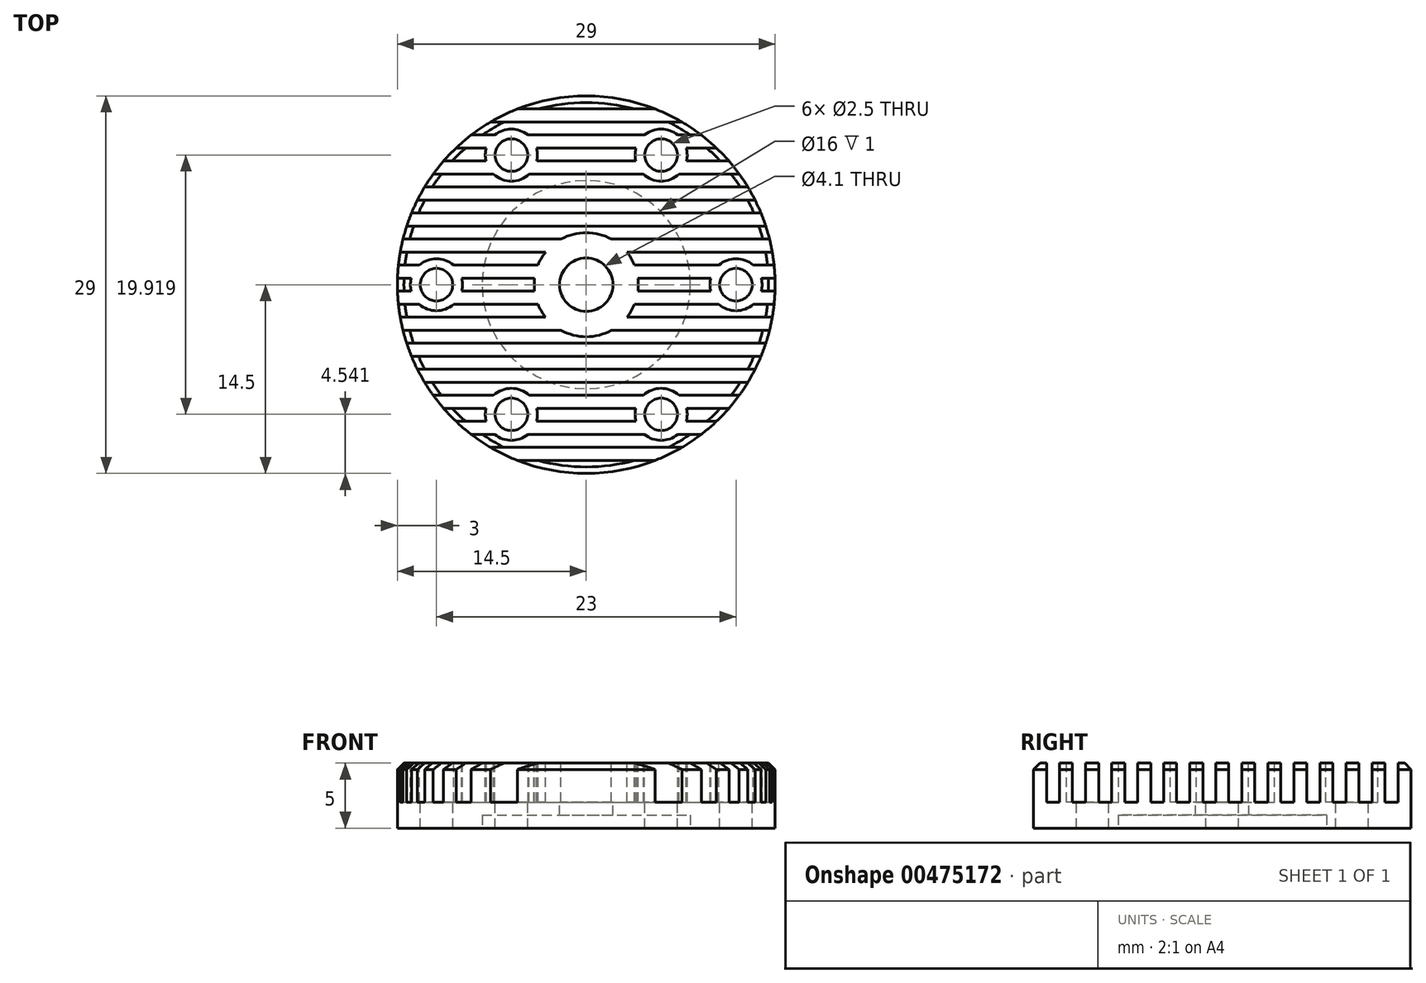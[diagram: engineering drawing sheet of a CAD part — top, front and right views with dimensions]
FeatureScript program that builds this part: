
annotation { "Feature Type Name" : "Feature", "Feature Type Description" : "" }
export const myFeature = defineFeature(function(context is Context, id is Id, definition is map)
    precondition{}
    {
        {
            var Q0;
            Q0=qCreatedBy(makeId("Top.planeOp"),FACE);
            var sketch = newSketch(context, id + "F0", { "sketchPlane" : qUnion([Q0])});
            skCircle(sketch, "E0", {"center": v(0, 0) * mm, "radius": 14.5 * mm});
            skSolve(sketch);
        }
        {
            var Q0;
            Q0 = qSketchRegion(id + "F0", true);
            extrude(context, id + "F1", {"entities" : qUnion([Q0]), "depth" : 5 * mm});
        }
        {
            var Q0;
            Q0=qCreatedBy(makeId("Right.planeOp"),FACE);
            var sketch = newSketch(context, id + "F2", { "sketchPlane" : qUnion([Q0])});
            skLineSegment(sketch, "E1", {"start": v(-0.5, 2) * mm, "end": v(-0.5, 5) * mm});
            skLineSegment(sketch, "E2", {"start": v(-0.5, 5) * mm, "end": v(0, 5) * mm});
            skLineSegment(sketch, "E3", {"start": v(-0.5, 2) * mm, "end": v(-1.5, 2) * mm});
            skLineSegment(sketch, "E4", {"start": v(-1.5, 2) * mm, "end": v(-1.5, 5) * mm});
            skLineSegment(sketch, "E5", {"start": v(-1.5, 5) * mm, "end": v(-2.5, 5) * mm});
            skLineSegment(sketch, "E6", {"start": v(-2.5, 5) * mm, "end": v(-2.5, 2) * mm});
            skLineSegment(sketch, "E7", {"start": v(-2.5, 2) * mm, "end": v(-3.5, 2) * mm});
            skLineSegment(sketch, "E8", {"start": v(-3.5, 2) * mm, "end": v(-3.5, 5) * mm});
            skLineSegment(sketch, "E9", {"start": v(-3.5, 5) * mm, "end": v(-4.5, 5) * mm});
            skLineSegment(sketch, "E10", {"start": v(-4.5, 5) * mm, "end": v(-4.5, 2) * mm});
            skLineSegment(sketch, "E11", {"start": v(-4.5, 2) * mm, "end": v(-5.5, 2) * mm});
            skLineSegment(sketch, "E12", {"start": v(-5.5, 2) * mm, "end": v(-5.5, 5) * mm});
            skLineSegment(sketch, "E13", {"start": v(-5.5, 5) * mm, "end": v(-6.5, 5) * mm});
            skLineSegment(sketch, "E14", {"start": v(-6.5, 5) * mm, "end": v(-6.5, 2) * mm});
            skLineSegment(sketch, "E15", {"start": v(-6.5, 2) * mm, "end": v(-7.5, 2) * mm});
            skLineSegment(sketch, "E16", {"start": v(-7.5, 2) * mm, "end": v(-7.5, 5) * mm});
            skLineSegment(sketch, "E17", {"start": v(-7.5, 5) * mm, "end": v(-8.5, 5) * mm});
            skLineSegment(sketch, "E18", {"start": v(-8.5, 5) * mm, "end": v(-8.5, 2) * mm});
            skLineSegment(sketch, "E19", {"start": v(-8.5, 2) * mm, "end": v(-9.5, 2) * mm});
            skLineSegment(sketch, "E20", {"start": v(-9.5, 2) * mm, "end": v(-9.5, 5) * mm});
            skLineSegment(sketch, "E21", {"start": v(-9.5, 5) * mm, "end": v(-10.5, 5) * mm});
            skLineSegment(sketch, "E22", {"start": v(-10.5, 5) * mm, "end": v(-10.5, 2) * mm});
            skLineSegment(sketch, "E23", {"start": v(-10.5, 2) * mm, "end": v(-11.5, 2) * mm});
            skLineSegment(sketch, "E24", {"start": v(-11.5, 2) * mm, "end": v(-11.5, 5) * mm});
            skLineSegment(sketch, "E25", {"start": v(-11.5, 5) * mm, "end": v(-12.5, 5) * mm});
            skLineSegment(sketch, "E26", {"start": v(-12.5, 5) * mm, "end": v(-12.5, 2) * mm});
            skLineSegment(sketch, "E27", {"start": v(-12.5, 2) * mm, "end": v(-13.5, 2) * mm});
            skLineSegment(sketch, "E28", {"start": v(-13.5, 2) * mm, "end": v(-13.5, 5) * mm});
            skLineSegment(sketch, "E29", {"start": v(-13.5, 5) * mm, "end": v(-12.5, 5) * mm});
            skLineSegment(sketch, "E30", {"start": v(-11.5, 5) * mm, "end": v(-10.5, 5) * mm});
            skLineSegment(sketch, "E31", {"start": v(-9.5, 5) * mm, "end": v(-8.5, 5) * mm});
            skLineSegment(sketch, "E32", {"start": v(-7.5, 5) * mm, "end": v(-6.5, 5) * mm});
            skLineSegment(sketch, "E33", {"start": v(-5.5, 5) * mm, "end": v(-4.5, 5) * mm});
            skLineSegment(sketch, "E34", {"start": v(-3.5, 5) * mm, "end": v(-2.5, 5) * mm});
            skLineSegment(sketch, "E35", {"start": v(-1.5, 5) * mm, "end": v(-0.5, 5) * mm});
            skLineSegment(sketch, "E36", {"start": v(0, 5) * mm, "end": v(0, 0) * mm, "construction": true});
            skLineSegment(sketch, "E37.MirrorCS", {"start": v(13.5, 5) * mm, "end": v(12.5, 5) * mm});
            skLineSegment(sketch, "E38.MirrorCS", {"start": v(13.5, 2) * mm, "end": v(13.5, 5) * mm});
            skLineSegment(sketch, "E39.MirrorCS", {"start": v(12.5, 2) * mm, "end": v(13.5, 2) * mm});
            skLineSegment(sketch, "E40.MirrorCS", {"start": v(12.5, 5) * mm, "end": v(12.5, 2) * mm});
            skLineSegment(sketch, "E41.MirrorCS", {"start": v(11.5, 5) * mm, "end": v(10.5, 5) * mm});
            skLineSegment(sketch, "E42.MirrorCS", {"start": v(11.5, 2) * mm, "end": v(11.5, 5) * mm});
            skLineSegment(sketch, "E43.MirrorCS", {"start": v(10.5, 2) * mm, "end": v(11.5, 2) * mm});
            skLineSegment(sketch, "E44.MirrorCS", {"start": v(10.5, 5) * mm, "end": v(10.5, 2) * mm});
            skLineSegment(sketch, "E45.MirrorCS", {"start": v(9.5, 5) * mm, "end": v(8.5, 5) * mm});
            skLineSegment(sketch, "E46.MirrorCS", {"start": v(9.5, 2) * mm, "end": v(9.5, 5) * mm});
            skLineSegment(sketch, "E47.MirrorCS", {"start": v(8.5, 2) * mm, "end": v(9.5, 2) * mm});
            skLineSegment(sketch, "E48.MirrorCS", {"start": v(8.5, 5) * mm, "end": v(8.5, 2) * mm});
            skLineSegment(sketch, "E49.MirrorCS", {"start": v(7.5, 5) * mm, "end": v(6.5, 5) * mm});
            skLineSegment(sketch, "E50.MirrorCS", {"start": v(7.5, 2) * mm, "end": v(7.5, 5) * mm});
            skLineSegment(sketch, "E51.MirrorCS", {"start": v(6.5, 2) * mm, "end": v(7.5, 2) * mm});
            skLineSegment(sketch, "E52.MirrorCS", {"start": v(6.5, 5) * mm, "end": v(6.5, 2) * mm});
            skLineSegment(sketch, "E53.MirrorCS", {"start": v(5.5, 5) * mm, "end": v(4.5, 5) * mm});
            skLineSegment(sketch, "E54.MirrorCS", {"start": v(5.5, 2) * mm, "end": v(5.5, 5) * mm});
            skLineSegment(sketch, "E55.MirrorCS", {"start": v(4.5, 2) * mm, "end": v(5.5, 2) * mm});
            skLineSegment(sketch, "E56.MirrorCS", {"start": v(4.5, 5) * mm, "end": v(4.5, 2) * mm});
            skLineSegment(sketch, "E57.MirrorCS", {"start": v(3.5, 5) * mm, "end": v(2.5, 5) * mm});
            skLineSegment(sketch, "E58.MirrorCS", {"start": v(3.5, 2) * mm, "end": v(3.5, 5) * mm});
            skLineSegment(sketch, "E59.MirrorCS", {"start": v(2.5, 2) * mm, "end": v(3.5, 2) * mm});
            skLineSegment(sketch, "E60.MirrorCS", {"start": v(2.5, 5) * mm, "end": v(2.5, 2) * mm});
            skLineSegment(sketch, "E61.MirrorCS", {"start": v(1.5, 5) * mm, "end": v(0.5, 5) * mm});
            skLineSegment(sketch, "E62.MirrorCS", {"start": v(1.5, 2) * mm, "end": v(1.5, 5) * mm});
            skLineSegment(sketch, "E63.MirrorCS", {"start": v(0.5, 2) * mm, "end": v(1.5, 2) * mm});
            skLineSegment(sketch, "E64.MirrorCS", {"start": v(0.5, 2) * mm, "end": v(0.5, 5) * mm});
            skSolve(sketch);
        }
        {
            var Q0;
            Q0 = qSketchRegion(id + "F2", true);
            extrude(context, id + "F3", {"entities" : qUnion([Q0]), "operationType" : NewBodyOperationType.REMOVE, "oppositeDirection" : true, "depth" : 30 * mm, "symmetric" : true});
        }
        {
            var Q0;
            Q0=makeQuery(id+"F1.opExtrude","CAP_FACE",FACE,{"disambiguationData":[OSD([sQuery(id+"F0.wireOp",EDGE,"E0")])],"isStart":true});
            var sketch = newSketch(context, id + "F4", { "sketchPlane" : qUnion([Q0])});
            skCircle(sketch, "E65", {"center": v(0, 0) * mm, "radius": 8 * mm});
            skSolve(sketch);
        }
        {
            var Q0;
            Q0=makeQuery(id+"F4.imprint","IMPRINT",FACE,{"disambiguationData":[TD([[makeQuery(id+"F4.imprint","IMPRINT",EDGE,{"derivedFrom":sQuery(id+"F4.wireOp",EDGE,"E65")}),1.0]])]});
            extrude(context, id + "F5", {"entities" : qUnion([Q0]), "operationType" : NewBodyOperationType.REMOVE, "oppositeDirection" : true, "depth" : 1 * mm});
        }
        {
            var Q0;
            {var subQ0=sQuery(id+"F0.wireOp",EDGE,"E0");Q0=makeQuery(id+"F3.boolean.opBoolean","SPLIT",FACE,{"disambiguationData":[TD([makeQuery(id+"F3.opExtrude","SWEPT_FACE",FACE,{"disambiguationData":[OSD([sQuery(id+"F2.wireOp",EDGE,"E1")])]})])],"derivedFrom":makeQuery(id+"F1.opExtrude","CAP_FACE",FACE,{"disambiguationData":[OSD([subQ0])],"isStart":false})});}
            var sketch = newSketch(context, id + "F6", { "sketchPlane" : qUnion([Q0])});
            skCircle(sketch, "E66", {"center": v(0, 0) * mm, "radius": 4 * mm});
            skSolve(sketch);
        }
        {
            var Q0;
            Q0 = qSketchRegion(id + "F6", true);
            extrude(context, id + "F7", {"entities" : qUnion([Q0]), "operationType" : NewBodyOperationType.REMOVE, "oppositeDirection" : true, "depth" : 3 * mm});
        }
        {
            var Q0;
            Q0=makeQuery(id+"F7.boolean.opBoolean","MERGE",FACE,{"derivedFrom":[makeQuery(id+"F3.boolean.opBoolean","COPY",FACE,{"derivedFrom":makeQuery(id+"F3.opExtrude","SWEPT_FACE",FACE,{"disambiguationData":[OSD([sQuery(id+"F2.wireOp",EDGE,"E3")])]})}),makeQuery(id+"F3.boolean.opBoolean","COPY",FACE,{"derivedFrom":makeQuery(id+"F3.opExtrude","SWEPT_FACE",FACE,{"disambiguationData":[OSD([sQuery(id+"F2.wireOp",EDGE,"E7")])]})}),makeQuery(id+"F3.boolean.opBoolean","COPY",FACE,{"derivedFrom":makeQuery(id+"F3.opExtrude","SWEPT_FACE",FACE,{"disambiguationData":[OSD([sQuery(id+"F2.wireOp",EDGE,"E59.MirrorCS")])]})}),makeQuery(id+"F3.boolean.opBoolean","COPY",FACE,{"derivedFrom":makeQuery(id+"F3.opExtrude","SWEPT_FACE",FACE,{"disambiguationData":[OSD([sQuery(id+"F2.wireOp",EDGE,"E63.MirrorCS")])]})}),makeQuery(id+"F7.opExtrude","CAP_FACE",FACE,{"disambiguationData":[OSD([sQuery(id+"F6.wireOp",EDGE,"E66")])],"isStart":false})]});
            var sketch = newSketch(context, id + "F8", { "sketchPlane" : qUnion([Q0])});
            skCircle(sketch, "E67", {"center": v(0, 0) * mm, "radius": 2.05 * mm});
            skSolve(sketch);
        }
        {
            var Q0;
            Q0=makeQuery(id+"F8.imprint","IMPRINT",FACE,{"disambiguationData":[TD([[makeQuery(id+"F8.imprint","IMPRINT",EDGE,{"derivedFrom":sQuery(id+"F8.wireOp",EDGE,"E67")}),1.0]])]});
            extrude(context, id + "F9", {"entities" : qUnion([Q0]), "operationType" : NewBodyOperationType.REMOVE, "oppositeDirection" : true, "depth" : 25 * mm});
        }
        {
            var Q0;
            {var subQ0=sQuery(id+"F0.wireOp",EDGE,"E0");Q0=makeQuery(id+"F7.boolean.opBoolean","SPLIT",FACE,{"disambiguationData":[OD(1.0)],"derivedFrom":makeQuery(id+"F3.boolean.opBoolean","SPLIT",FACE,{"disambiguationData":[TD([makeQuery(id+"F3.opExtrude","SWEPT_FACE",FACE,{"disambiguationData":[OSD([sQuery(id+"F2.wireOp",EDGE,"E4")])]})])],"derivedFrom":makeQuery(id+"F1.opExtrude","CAP_FACE",FACE,{"disambiguationData":[OSD([subQ0])],"isStart":false})})});}
            var sketch = newSketch(context, id + "F10", { "sketchPlane" : qUnion([Q0])});
            skCircle(sketch, "E68", {"center": v(0, 0) * mm, "radius": 11.5 * mm, "construction": true});
            skLineSegment(sketch, "E69", {"start": v(0, 0) * mm, "end": v(0, 17.47) * mm, "construction": true});
            skLineSegment(sketch, "E70", {"start": v(0, 0) * mm, "end": v(5.75, 9.96) * mm});
            skCircle(sketch, "E71", {"center": v(5.75, 9.96) * mm, "radius": 2 * mm});
            skCircle(sketch, "E72.1.0", {"center": v(-5.75, 9.96) * mm, "radius": 2 * mm});
            skCircle(sketch, "E72.2.0", {"center": v(-11.5, 0) * mm, "radius": 2 * mm});
            skCircle(sketch, "E72.3.0", {"center": v(-5.75, -9.96) * mm, "radius": 2 * mm});
            skCircle(sketch, "E72.4.0", {"center": v(5.75, -9.96) * mm, "radius": 2 * mm});
            skCircle(sketch, "E72.5.0", {"center": v(11.5, 0) * mm, "radius": 2 * mm});
            skSolve(sketch);
        }
        {
            var Q0;
            Q0 = qSketchRegion(id + "F10", true);
            extrude(context, id + "F11", {"entities" : qUnion([Q0]), "operationType" : NewBodyOperationType.REMOVE, "oppositeDirection" : true, "depth" : 3 * mm});
        }
        {
            var Q0;
            Q0=makeQuery(id+"F11.boolean.opBoolean","MERGE",FACE,{"derivedFrom":[makeQuery(id+"F3.boolean.opBoolean","COPY",FACE,{"derivedFrom":makeQuery(id+"F3.opExtrude","SWEPT_FACE",FACE,{"disambiguationData":[OSD([sQuery(id+"F2.wireOp",EDGE,"E43.MirrorCS")])]})}),makeQuery(id+"F3.boolean.opBoolean","COPY",FACE,{"derivedFrom":makeQuery(id+"F3.opExtrude","SWEPT_FACE",FACE,{"disambiguationData":[OSD([sQuery(id+"F2.wireOp",EDGE,"E47.MirrorCS")])]})}),makeQuery(id+"F11.opExtrude","CAP_FACE",FACE,{"disambiguationData":[OSD([sQuery(id+"F10.wireOp",EDGE,"E71")])],"isStart":false}),makeQuery(id+"F11.opExtrude","CAP_FACE",FACE,{"disambiguationData":[OSD([sQuery(id+"F10.wireOp",EDGE,"E72.1.0")])],"isStart":false})]});
            var sketch = newSketch(context, id + "F12", { "sketchPlane" : qUnion([Q0])});
            skCircle(sketch, "E73", {"center": v(5.75, 9.96) * mm, "radius": 1.25 * mm});
            skCircle(sketch, "E74.1.0", {"center": v(-5.75, 9.96) * mm, "radius": 1.25 * mm});
            skCircle(sketch, "E74.2.0", {"center": v(-11.5, 0) * mm, "radius": 1.25 * mm});
            skCircle(sketch, "E74.3.0", {"center": v(-5.75, -9.96) * mm, "radius": 1.25 * mm});
            skCircle(sketch, "E74.4.0", {"center": v(5.75, -9.96) * mm, "radius": 1.25 * mm});
            skCircle(sketch, "E74.5.0", {"center": v(11.5, 0) * mm, "radius": 1.25 * mm});
            skPoint(sketch, "E74.center", {"position": v(0, 0) * mm});
            skSolve(sketch);
        }
        {
            var Q0;
            Q0 = qSketchRegion(id + "F12", true);
            extrude(context, id + "F13", {"entities" : qUnion([Q0]), "operationType" : NewBodyOperationType.REMOVE, "oppositeDirection" : true, "depth" : 25 * mm});
        }
        {
            var Q0;
            Q0=qCreatedBy(makeId("Front.planeOp"),FACE);
            var sketch = newSketch(context, id + "F14", { "sketchPlane" : qUnion([Q0])});
            skLineSegment(sketch, "E75", {"start": v(14, 5) * mm, "end": v(14.5, 4.5) * mm});
            skLineSegment(sketch, "E76", {"start": v(14.5, 4.5) * mm, "end": v(14.5, 5) * mm});
            skLineSegment(sketch, "E77", {"start": v(14.5, 5) * mm, "end": v(14, 5) * mm});
            skSolve(sketch);
        }
        {
            var Q0;
            Q0 = qSketchRegion(id + "F14", true);
            var Q1;
            Q1=makeQuery(id+"F1.opExtrude","CAP_EDGE",EDGE,{"disambiguationData":[OSD([sQuery(id+"F0.wireOp",EDGE,"E0")])],"isStart":true});
            revolve(context, id + "F15", {"operationType" : NewBodyOperationType.REMOVE, "entities" : qUnion([Q0]), "axis" : qUnion([Q1]), "revolveType" : RevolveType.FULL, "oppositeDirection" : true});
        }
    });
